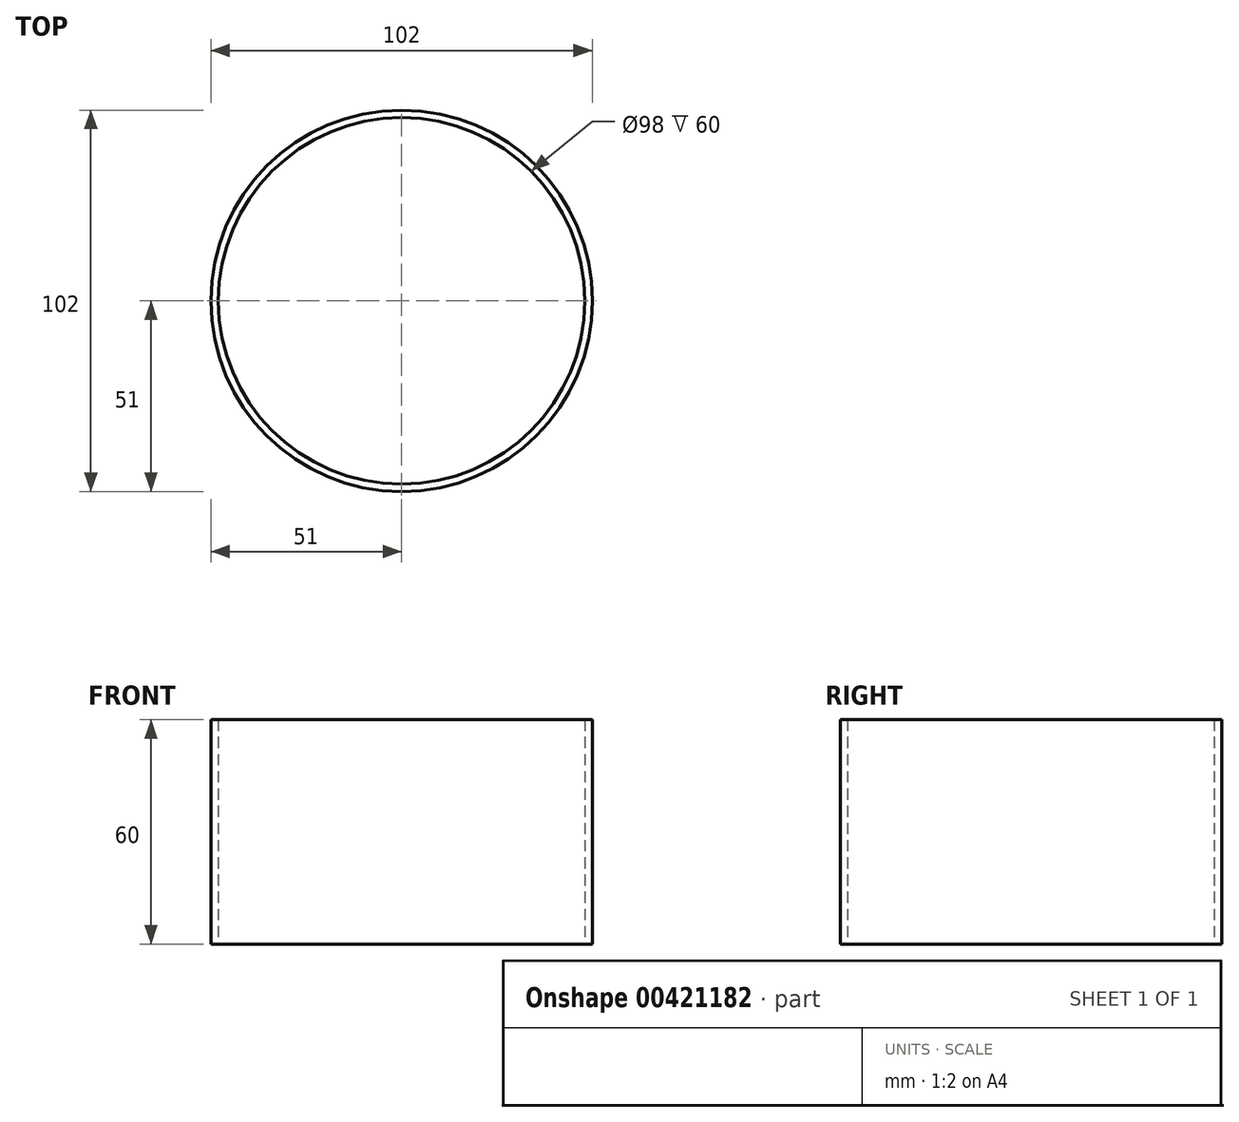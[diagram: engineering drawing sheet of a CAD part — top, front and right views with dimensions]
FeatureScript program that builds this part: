
annotation { "Feature Type Name" : "Feature", "Feature Type Description" : "" }
export const myFeature = defineFeature(function(context is Context, id is Id, definition is map)
    precondition{}
    {
        {
            var Q0;
            Q0=qCreatedBy(makeId("Top.planeOp"),FACE);
            var sketch = newSketch(context, id + "F0", { "sketchPlane" : qUnion([Q0])});
            skCircle(sketch, "E0", {"center": v(0, 0) * mm, "radius": 49 * mm});
            skCircle(sketch, "E1", {"center": v(0, 0) * mm, "radius": 51 * mm});
            skSolve(sketch);
        }
        {
            var Q0;
            Q0 = qSketchRegion(id + "F0", true);
            extrude(context, id + "F1", {"entities" : qUnion([Q0]), "depth" : 60 * mm});
        }
    });
